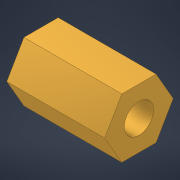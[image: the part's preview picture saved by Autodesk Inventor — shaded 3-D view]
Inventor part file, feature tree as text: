
AUTODESK INVENTOR PART (.ipt)
format: ipt  version: 2022 (Build 260153000, 153)  size: 97,792 bytes
history: native  units: mm
features: extrude x1, sketch x1
ambient origin geometry x8: Origin, YZ Plane, XZ Plane, XY Plane, X Axis, Y Axis, Z Axis, Center Point
bodies: Solid1 (feature_tree)
feature tree (2):
  extrude  "Extrusion1"  Depth=6.062178mm
  sketch  "Sketch1"  dims[d0=7.0mm d1=3.0mm d2=10.0mm d3=0.0mm d4=6.062178mm]
